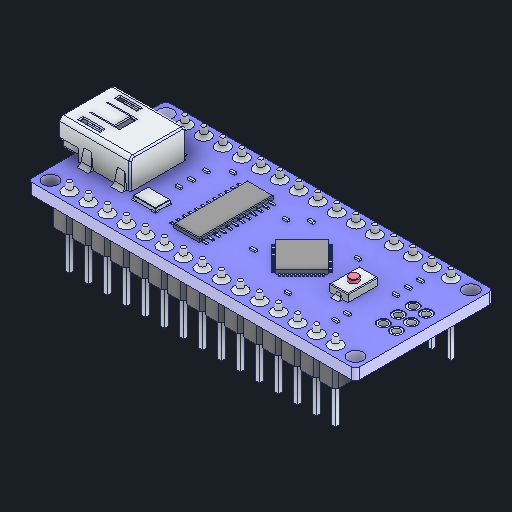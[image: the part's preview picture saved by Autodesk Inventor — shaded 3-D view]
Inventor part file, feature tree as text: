
AUTODESK INVENTOR PART (.ipt)
format: ipt  version: 2024.1 (Build 281209000, 209)  size: 991,232 bytes
history: native  units: in
note: dims shown in document units (in); Inventor stores cm internally (conversion verified against a paired STEP export)
features: sketch x1
ambient origin geometry x8: Origin, YZ Plane, XZ Plane, XY Plane, X Axis, Y Axis, Z Axis, Center Point
bodies: Solid1 (feature_tree)
feature tree (1):
  sketch  "Sketch-Pattern1"
